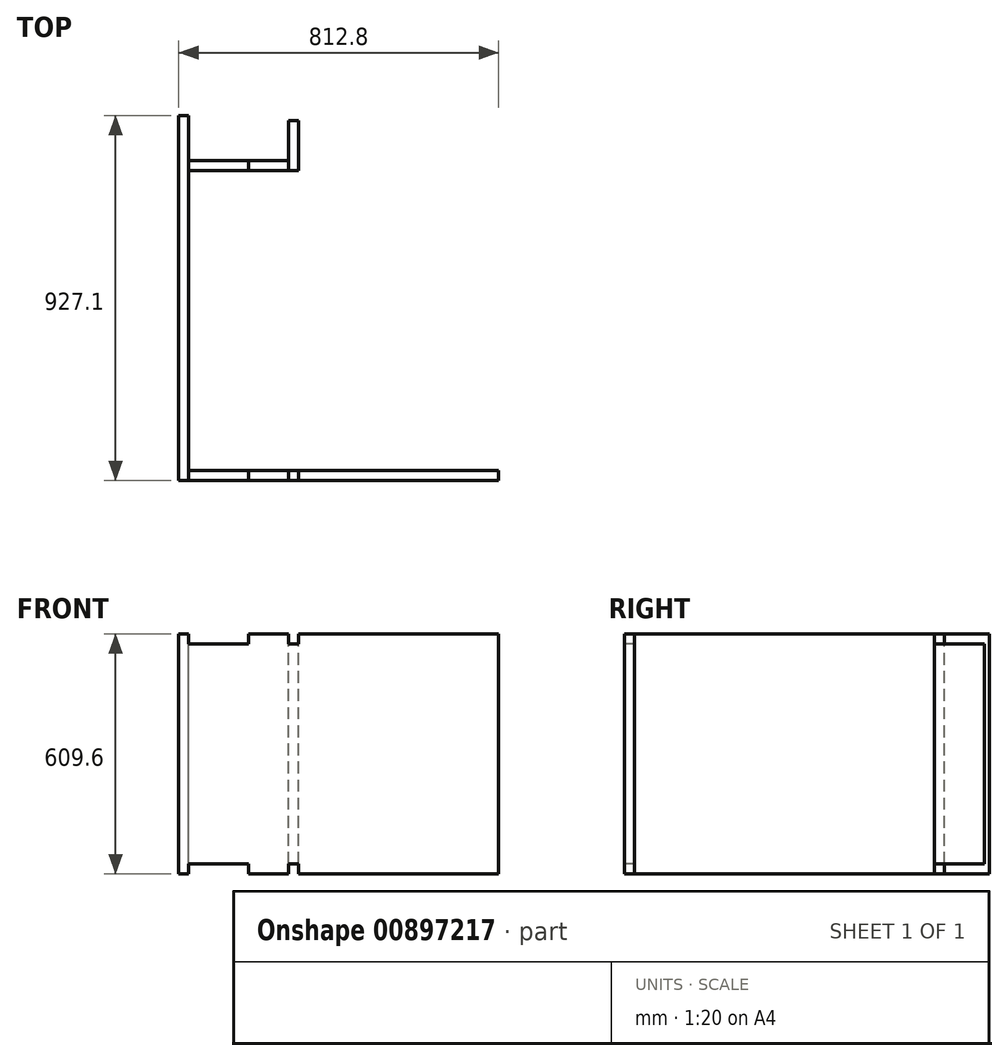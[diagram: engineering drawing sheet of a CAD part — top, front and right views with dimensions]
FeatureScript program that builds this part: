
annotation { "Feature Type Name" : "Feature", "Feature Type Description" : "" }
export const myFeature = defineFeature(function(context is Context, id is Id, definition is map)
    precondition{}
    {
        {
            var Q0;
            Q0=qCreatedBy(makeId("Top.planeOp"),FACE);
            var sketch = newSketch(context, id + "F0", { "sketchPlane" : qUnion([Q0])});
            skLineSegment(sketch, "E0.top", {"start": v(0, 812.8) * mm, "end": v(304.8, 812.8) * mm});
            skLineSegment(sketch, "E1", {"start": v(25.4, 787.4) * mm, "end": v(304.8, 787.4) * mm});
            skPoint(sketch, "E0.bottom.start.orphan", {"position": v(0, 0) * mm});
            skLineSegment(sketch, "E2.trimOffspring", {"start": v(304.8, 787.4) * mm, "end": v(304.8, 812.8) * mm});
            skLineSegment(sketch, "E3", {"start": v(25.4, 25.4) * mm, "end": v(812.8, 25.4) * mm});
            skLineSegment(sketch, "E4", {"start": v(812.8, 25.4) * mm, "end": v(812.8, 0) * mm});
            skLineSegment(sketch, "E5", {"start": v(812.8, 0) * mm, "end": v(0, 0) * mm});
            skLineSegment(sketch, "E6", {"start": v(25.4, 787.4) * mm, "end": v(25.4, 25.4) * mm});
            skLineSegment(sketch, "E7", {"start": v(0, 812.8) * mm, "end": v(0, 0) * mm});
            skLineSegment(sketch, "E8", {"start": v(0, 406.4) * mm, "end": v(763.61, 406.4) * mm, "construction": true});
            skSolve(sketch);
        }
        {
            var Q0;
            Q0=qSketchRegion(id+"F0",true);
            extrude(context, id + "F1", {"entities" : qUnion([Q0]), "oppositeDirection" : true, "depth" : 609.6 * mm, "offsetDistance" : 25.4 * mm});
        }
        {
            var Q0;
            Q0=makeQuery(id+"F0.imprint","IMPRINT",FACE,{"disambiguationData":[TD([[makeQuery(id+"F0.imprint","IMPRINT",EDGE,{"derivedFrom":sQuery(id+"F0.wireOp",EDGE,"E0.top")}),-1.0]])]});
            var sketch = newSketch(context, id + "F2", { "sketchPlane" : qUnion([Q0])});
            skLineSegment(sketch, "E9.bottom", {"start": v(304.8, 812.8) * mm, "end": v(279.4, 812.8) * mm});
            skLineSegment(sketch, "E9.top", {"start": v(304.8, 914.4) * mm, "end": v(279.4, 914.4) * mm});
            skLineSegment(sketch, "E9.left", {"start": v(304.8, 812.8) * mm, "end": v(304.8, 914.4) * mm});
            skLineSegment(sketch, "E9.right", {"start": v(279.4, 812.8) * mm, "end": v(279.4, 914.4) * mm});
            skLineSegment(sketch, "E10.bottom", {"start": v(0, 812.8) * mm, "end": v(25.4, 812.8) * mm});
            skLineSegment(sketch, "E10.top", {"start": v(0, 927.1) * mm, "end": v(25.4, 927.1) * mm});
            skLineSegment(sketch, "E10.left", {"start": v(0, 812.8) * mm, "end": v(0, 927.1) * mm});
            skLineSegment(sketch, "E10.right", {"start": v(25.4, 812.8) * mm, "end": v(25.4, 927.1) * mm});
            skLineSegment(sketch, "E11.MirrorCS", {"start": v(0, -114.3) * mm, "end": v(25.4, -114.3) * mm, "construction": true});
            skLineSegment(sketch, "E12.MirrorCS", {"start": v(304.8, -101.6) * mm, "end": v(279.4, -101.6) * mm, "construction": true});
            skLineSegment(sketch, "E13.MirrorCS", {"start": v(0, 0) * mm, "end": v(0, -114.3) * mm, "construction": true});
            skLineSegment(sketch, "E14.MirrorCS", {"start": v(304.8, 0) * mm, "end": v(279.4, 0) * mm, "construction": true});
            skLineSegment(sketch, "E15.MirrorCS", {"start": v(0, 0) * mm, "end": v(25.4, 0) * mm, "construction": true});
            skLineSegment(sketch, "E16.MirrorCS", {"start": v(304.8, 0) * mm, "end": v(304.8, -101.6) * mm, "construction": true});
            skLineSegment(sketch, "E17.MirrorCS", {"start": v(279.4, 0) * mm, "end": v(279.4, -101.6) * mm, "construction": true});
            skLineSegment(sketch, "E18.MirrorCS", {"start": v(25.4, 0) * mm, "end": v(25.4, -114.3) * mm, "construction": true});
            skSolve(sketch);
        }
        {
            var Q0;
            Q0=qSketchRegion(id+"F2",true);
            extrude(context, id + "F3", {"entities" : qUnion([Q0]), "operationType" : NewBodyOperationType.ADD, "oppositeDirection" : true, "depth" : 609.6 * mm, "offsetDistance" : 25.4 * mm});
        }
        {
            var Q0;
            Q0=qCreatedBy(makeId("Front.planeOp"),FACE);
            var sketch = newSketch(context, id + "F4", { "sketchPlane" : qUnion([Q0])});
            skLineSegment(sketch, "E19.bottom", {"start": v(25.4, 0) * mm, "end": v(177.8, 0) * mm});
            skLineSegment(sketch, "E19.top", {"start": v(25.4, -25.4) * mm, "end": v(177.8, -25.4) * mm});
            skLineSegment(sketch, "E19.left", {"start": v(25.4, 0) * mm, "end": v(25.4, -25.4) * mm});
            skLineSegment(sketch, "E19.right", {"start": v(177.8, 0) * mm, "end": v(177.8, -25.4) * mm});
            skLineSegment(sketch, "E20.direction1", {"start": v(25.4, -25.4) * mm, "end": v(50.8, -25.4) * mm, "construction": true});
            skLineSegment(sketch, "E21.bottom", {"start": v(304.8, 0) * mm, "end": v(279.4, 0) * mm});
            skLineSegment(sketch, "E21.top", {"start": v(304.8, -25.4) * mm, "end": v(279.4, -25.4) * mm});
            skLineSegment(sketch, "E21.left", {"start": v(304.8, 0) * mm, "end": v(304.8, -25.4) * mm});
            skLineSegment(sketch, "E21.right", {"start": v(279.4, 0) * mm, "end": v(279.4, -25.4) * mm});
            skLineSegment(sketch, "E22.bottom", {"start": v(25.4, -609.6) * mm, "end": v(177.8, -609.6) * mm});
            skLineSegment(sketch, "E22.top", {"start": v(25.4, -584.2) * mm, "end": v(177.8, -584.2) * mm});
            skLineSegment(sketch, "E22.left", {"start": v(25.4, -609.6) * mm, "end": v(25.4, -584.2) * mm});
            skLineSegment(sketch, "E22.right", {"start": v(177.8, -609.6) * mm, "end": v(177.8, -584.2) * mm});
            skLineSegment(sketch, "E23.bottom", {"start": v(304.8, -584.2) * mm, "end": v(279.4, -584.2) * mm});
            skLineSegment(sketch, "E23.top", {"start": v(304.8, -609.6) * mm, "end": v(279.4, -609.6) * mm});
            skLineSegment(sketch, "E23.left", {"start": v(304.8, -609.6) * mm, "end": v(304.8, -584.2) * mm});
            skLineSegment(sketch, "E23.right", {"start": v(279.4, -609.6) * mm, "end": v(279.4, -584.2) * mm});
            skSolve(sketch);
        }
        {
            var Q0;
            Q0=qSketchRegion(id+"F4",true);
            extrude(context, id + "F5", {"entities" : qUnion([Q0]), "operationType" : NewBodyOperationType.REMOVE, "oppositeDirection" : true, "depth" : 2032 * mm, "offsetDistance" : 25.4 * mm, "symmetric" : true});
        }
    });
